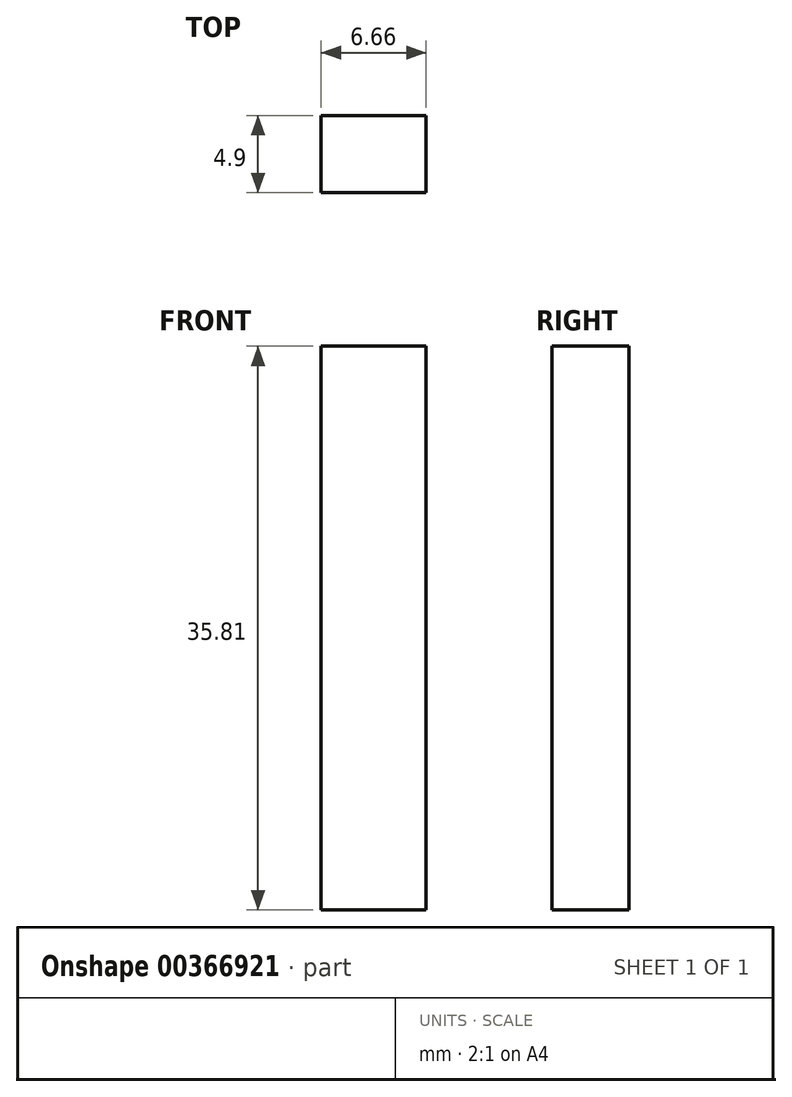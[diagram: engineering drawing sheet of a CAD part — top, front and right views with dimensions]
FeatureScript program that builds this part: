
annotation { "Feature Type Name" : "Feature", "Feature Type Description" : "" }
export const myFeature = defineFeature(function(context is Context, id is Id, definition is map)
    precondition{}
    {
        {
            var Q0;
            Q0=qCreatedBy(makeId("Top.planeOp"),FACE);
            var sketch = newSketch(context, id + "F0", { "sketchPlane" : qUnion([Q0])});
            skLineSegment(sketch, "E0.bottom", {"start": v(-3.33, -2.45) * mm, "end": v(3.33, -2.45) * mm});
            skLineSegment(sketch, "E0.top", {"start": v(-3.33, 2.45) * mm, "end": v(3.33, 2.45) * mm});
            skLineSegment(sketch, "E0.left", {"start": v(-3.33, -2.45) * mm, "end": v(-3.33, 2.45) * mm});
            skLineSegment(sketch, "E0.right", {"start": v(3.33, -2.45) * mm, "end": v(3.33, 2.45) * mm});
            skPoint(sketch, "E0.middle", {"position": v(0, 0) * mm});
            skSolve(sketch);
        }
        {
            var Q0;
            Q0=makeQuery(id+"F0.imprint","IMPRINT",FACE,{"disambiguationData":[TD([[makeQuery(id+"F0.imprint","IMPRINT",EDGE,{"derivedFrom":sQuery(id+"F0.wireOp",EDGE,"E0.bottom")}),1.0]])]});
            extrude(context, id + "F1", {"entities" : qUnion([Q0]), "depth" : 35.81 * mm});
        }
    });
